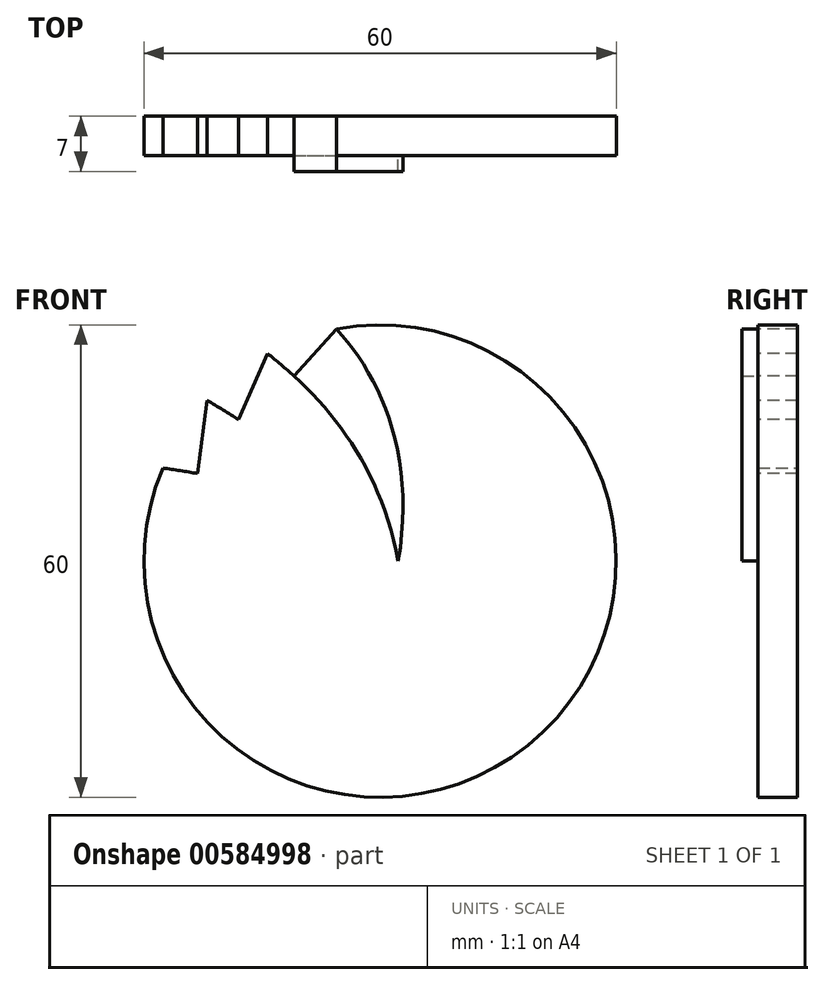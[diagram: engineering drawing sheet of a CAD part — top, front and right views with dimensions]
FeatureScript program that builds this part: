
annotation { "Feature Type Name" : "Feature", "Feature Type Description" : "" }
export const myFeature = defineFeature(function(context is Context, id is Id, definition is map)
    precondition{}
    {
        {
            var Q0;
            Q0=qCreatedBy(makeId("Front.planeOp"),FACE);
            var sketch = newSketch(context, id + "F0", { "sketchPlane" : qUnion([Q0])});
            skCircle(sketch, "E0", {"center": v(0, 0) * mm, "radius": 30 * mm});
            skSolve(sketch);
        }
        {
            var Q0;
            Q0=makeQuery(id+"F0.imprint","IMPRINT",FACE,{"disambiguationData":[TD([[makeQuery(id+"F0.imprint","IMPRINT",EDGE,{"derivedFrom":sQuery(id+"F0.wireOp",EDGE,"E0")}),1.0]])]});
            extrude(context, id + "F1", {"entities" : qUnion([Q0]), "depth" : 5 * mm, "offsetDistance" : 25 * mm});
        }
        {
            var Q0;
            Q0=makeQuery(id+"F1.opExtrude","CAP_FACE",FACE,{"disambiguationData":[OSD([sQuery(id+"F0.wireOp",EDGE,"E0")])],"isStart":false});
            var sketch = newSketch(context, id + "F2", { "sketchPlane" : qUnion([Q0])});
            skCircle(sketch, "E1", {"center": v(0, 0) * mm, "radius": 1.97 * mm});
            skSolve(sketch);
        }
        {
            var Q0;
            Q0=makeQuery(id+"F2.imprint","IMPRINT",FACE,{"disambiguationData":[TD([[makeQuery(id+"F2.imprint","IMPRINT",EDGE,{"derivedFrom":sQuery(id+"F2.wireOp",EDGE,"E1")}),-1.0]])]});
            var sketch = newSketch(context, id + "F3", { "sketchPlane" : qUnion([Q0])});
            skFitSpline(sketch, "E2", {"points": [v(-5.54, 29.48) * mm, v(2.3, 0) * mm], "startDerivative": vector(16.62, -17.95) * mm, "endDerivative": vector(-6.97, -40.1) * mm});
            skFitSpline(sketch, "E3", {"points": [v(-14.3, 26.37) * mm, v(2.3, 0) * mm], "startDerivative": vector(23, -18.1) * mm, "endDerivative": vector(6.9, -36.9) * mm});
            skLineSegment(sketch, "E4", {"start": v(-5.54, 29.48) * mm, "end": v(-10.93, 23.5) * mm});
            skFitSpline(sketch, "E5", {"points": [v(-21.98, 20.41) * mm, v(2.3, 0) * mm], "startDerivative": vector(26.32, -15.76) * mm, "endDerivative": vector(19.1, -28.52) * mm});
            skLineSegment(sketch, "E6", {"start": v(-14.3, 26.37) * mm, "end": v(-17.95, 17.96) * mm});
            skFitSpline(sketch, "E7", {"points": [v(-27.57, 11.82) * mm, v(0, 2.93) * mm], "startDerivative": vector(23.17, -3.3) * mm, "endDerivative": vector(25.78, -16.67) * mm});
            skLineSegment(sketch, "E8", {"start": v(-21.98, 20.41) * mm, "end": v(-23.18, 11.11) * mm});
            skFitSpline(sketch, "E9", {"points": [v(-29.95, 1.78) * mm, v(0, 2.93) * mm], "startDerivative": vector(32.09, 8.93) * mm, "endDerivative": vector(31.83, -6.67) * mm});
            skLineSegment(sketch, "E10", {"start": v(-27.57, 11.82) * mm, "end": v(-25.79, 2.83) * mm});
            skFitSpline(sketch, "E11", {"points": [v(-29.08, -7.36) * mm, v(0, 2.93) * mm], "startDerivative": vector(26.76, 22.09) * mm, "endDerivative": vector(32.01, 8.79) * mm});
            skLineSegment(sketch, "E12", {"start": v(-29.95, 1.78) * mm, "end": v(-26.03, -5.13) * mm});
            skSolve(sketch);
        }
        {
            var Q0;
            {var subQ3=sQuery(id+"F3.wireOp",EDGE,"E4");Q0=makeQuery(id+"F3.imprint","IMPRINT",FACE,{"disambiguationData":[TD([[makeQuery(id+"F3.imprint","IMPRINT",EDGE,{"derivedFrom":subQ3}),-1.0]])]});}
            extrude(context, id + "F4", {"entities" : qUnion([Q0]), "operationType" : NewBodyOperationType.REMOVE, "oppositeDirection" : true, "depth" : 5 * mm, "offsetDistance" : 25 * mm});
        }
        {
            var Q0;
            {var subQ3=sQuery(id+"F3.wireOp",EDGE,"E6");Q0=makeQuery(id+"F3.imprint","IMPRINT",FACE,{"disambiguationData":[TD([[makeQuery(id+"F3.imprint","IMPRINT",EDGE,{"derivedFrom":subQ3}),-1.0]])]});}
            extrude(context, id + "F5", {"entities" : qUnion([Q0]), "operationType" : NewBodyOperationType.REMOVE, "oppositeDirection" : true, "depth" : 5 * mm, "offsetDistance" : 25 * mm});
        }
        {
            var Q0;
            {var subQ3=sQuery(id+"F3.wireOp",EDGE,"E8");Q0=makeQuery(id+"F3.imprint","IMPRINT",FACE,{"disambiguationData":[TD([[makeQuery(id+"F3.imprint","IMPRINT",EDGE,{"derivedFrom":subQ3}),-1.0]])]});}
            extrude(context, id + "F6", {"entities" : qUnion([Q0]), "operationType" : NewBodyOperationType.REMOVE, "oppositeDirection" : true, "depth" : 5 * mm, "offsetDistance" : 25 * mm});
        }
        {
            var Q0;
            {var subQ0=sQuery(id+"F3.wireOp",EDGE,"E2");Q0=makeQuery(id+"F3.imprint","IMPRINT",FACE,{"disambiguationData":[TD([[makeQuery(id+"F3.imprint","IMPRINT",EDGE,{"derivedFrom":subQ0}),-1.0]])]});}
            extrude(context, id + "F7", {"entities" : qUnion([Q0]), "operationType" : NewBodyOperationType.ADD, "depth" : 2 * mm, "offsetDistance" : 25 * mm});
        }
    });
